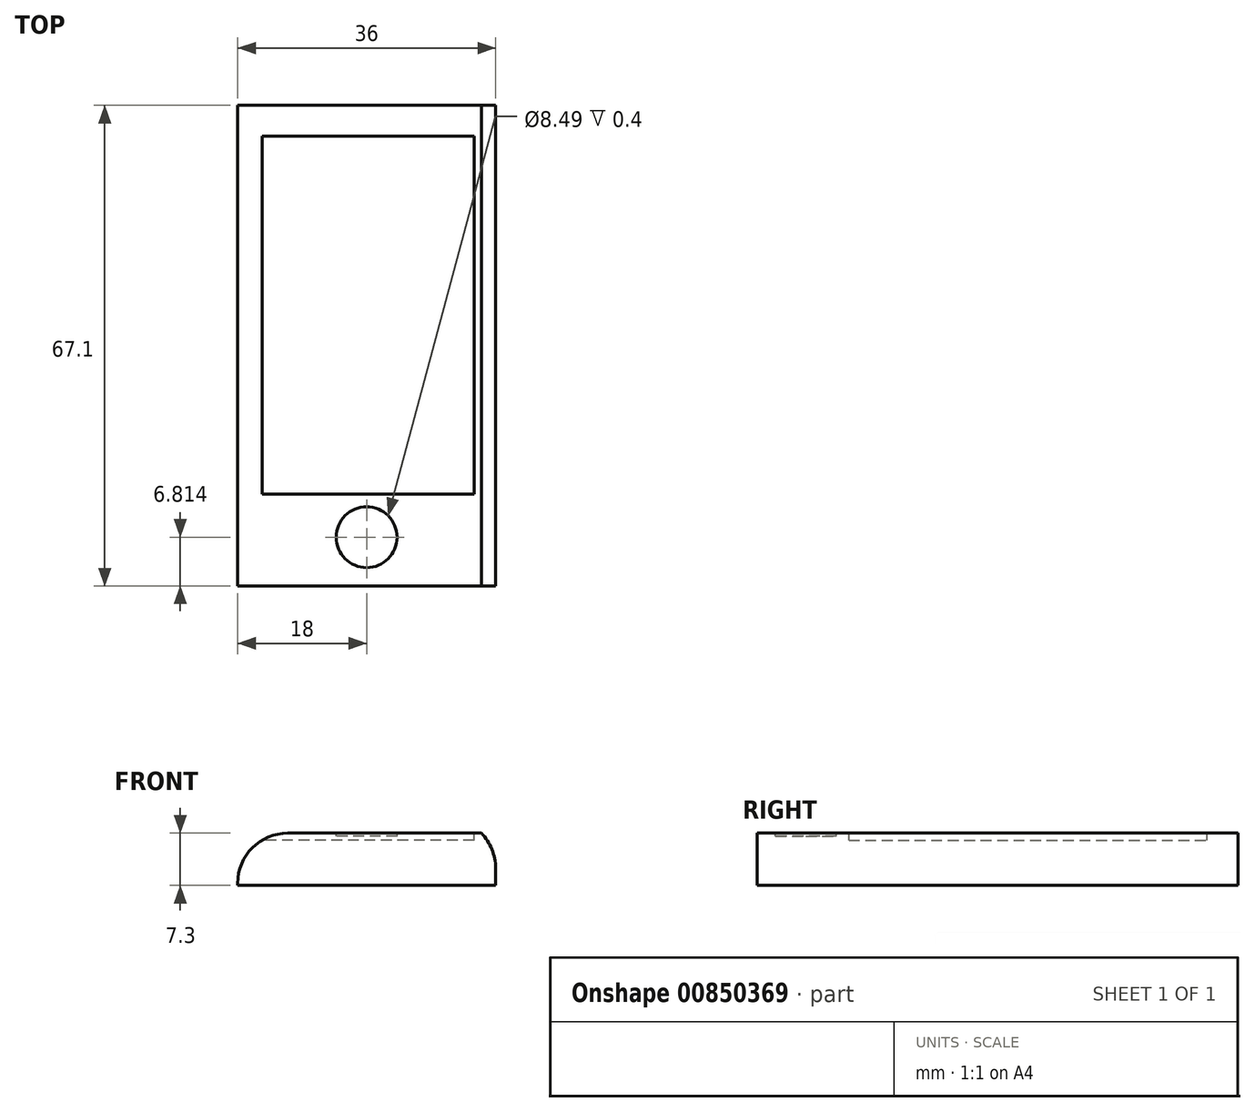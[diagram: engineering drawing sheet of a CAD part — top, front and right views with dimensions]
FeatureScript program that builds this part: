
annotation { "Feature Type Name" : "Feature", "Feature Type Description" : "" }
export const myFeature = defineFeature(function(context is Context, id is Id, definition is map)
    precondition{}
    {
        {
            var Q0;
            Q0=qCreatedBy(makeId("Top.planeOp"),FACE);
            var sketch = newSketch(context, id + "F0", { "sketchPlane" : qUnion([Q0])});
            skLineSegment(sketch, "E0.bottom", {"start": v(-18, 33.55) * mm, "end": v(18, 33.55) * mm});
            skLineSegment(sketch, "E0.top", {"start": v(-18, -33.55) * mm, "end": v(18, -33.55) * mm});
            skLineSegment(sketch, "E0.left", {"start": v(-18, 33.55) * mm, "end": v(-18, -33.55) * mm});
            skLineSegment(sketch, "E0.right", {"start": v(18, 33.55) * mm, "end": v(18, -33.55) * mm});
            skPoint(sketch, "E0.middle", {"position": v(0, 0) * mm});
            skSolve(sketch);
        }
        {
            var Q0;
            Q0=qSketchRegion(id+"F0",true);
            extrude(context, id + "F1", {"entities" : qUnion([Q0]), "depth" : 7.3 * mm, "offsetDistance" : 25 * mm});
        }
        {
            var Q0;
            Q0=makeQuery(id+"F1.opExtrude","CAP_FACE",FACE,{"disambiguationData":[OSD([sQuery(id+"F0.wireOp",EDGE,"E0.bottom"),sQuery(id+"F0.wireOp",EDGE,"E0.top"),sQuery(id+"F0.wireOp",EDGE,"E0.left"),sQuery(id+"F0.wireOp",EDGE,"E0.right")])],"isStart":false});
            var sketch = newSketch(context, id + "F2", { "sketchPlane" : qUnion([Q0])});
            skCircle(sketch, "E1", {"center": v(0, -26.74) * mm, "radius": 4.25 * mm});
            skSolve(sketch);
        }
        {
            var Q0;
            Q0=qSketchRegion(id+"F2",true);
            extrude(context, id + "F3", {"entities" : qUnion([Q0]), "operationType" : NewBodyOperationType.REMOVE, "oppositeDirection" : true, "depth" : 0.4 * mm, "offsetDistance" : 25 * mm});
        }
        {
            var Q0;
            Q0=makeQuery(id+"F2.imprint","IMPRINT",FACE,{"disambiguationData":[TD([[makeQuery(id+"F2.imprint","IMPRINT",EDGE,{"derivedFrom":sQuery(id+"F2.wireOp",EDGE,"E1")}),-1.0]])]});
            var sketch = newSketch(context, id + "F4", { "sketchPlane" : qUnion([Q0])});
            skLineSegment(sketch, "E2.bottom", {"start": v(15, -20.74) * mm, "end": v(-15, -20.74) * mm});
            skLineSegment(sketch, "E2.top", {"start": v(15, 29.26) * mm, "end": v(-15, 29.26) * mm});
            skLineSegment(sketch, "E2.left", {"start": v(15, -20.74) * mm, "end": v(15, 29.26) * mm});
            skLineSegment(sketch, "E2.right", {"start": v(-15, -20.74) * mm, "end": v(-15, 29.26) * mm});
            skPoint(sketch, "E2.middle", {"position": v(0, 4.26) * mm});
            skSolve(sketch);
        }
        {
            var Q0;
            Q0=makeQuery(id+"F1.opExtrude","CAP_EDGE",EDGE,{"disambiguationData":[OSD([sQuery(id+"F0.wireOp",EDGE,"E0.right")])],"isStart":false});
            chamfer(context, id + "F5", {"entities" : qUnion([Q0]), "width" : 2 * mm, "tangentPropagation" : true});
        }
        {
            var Q0;
            {var subQ0=sQuery(id+"F0.wireOp",EDGE,"E0.right");Q0=makeQuery(id+"F5.opChamfer","BLEND_EDGE",EDGE,{"blendedFrom":[makeQuery(id+"F1.opExtrude","CAP_EDGE",EDGE,{"disambiguationData":[OSD([subQ0])],"isStart":false}),makeQuery(id+"F1.opExtrude","SWEPT_FACE",FACE,{"disambiguationData":[OSD([subQ0])]})],"blendedInto":[makeQuery(id+"F1.opExtrude","SWEPT_FACE",FACE,{"disambiguationData":[OSD([subQ0])]})]});}
            fillet(context, id + "F6", {"entities" : qUnion([Q0]), "radius" : 7 * mm, "tangentPropagation" : true, "allowEdgeOverflow" : false});
        }
        {
            var Q0;
            Q0=qSketchRegion(id+"F4",true);
            extrude(context, id + "F7", {"entities" : qUnion([Q0]), "operationType" : NewBodyOperationType.REMOVE, "oppositeDirection" : true, "depth" : 1 * mm, "offsetDistance" : 25 * mm});
        }
        {
            var Q0;
            Q0=makeQuery(id+"F1.opExtrude","CAP_EDGE",EDGE,{"disambiguationData":[OSD([sQuery(id+"F0.wireOp",EDGE,"E0.left")])],"isStart":false});
            fillet(context, id + "F8", {"entities" : qUnion([Q0]), "radius" : 7 * mm, "tangentPropagation" : true, "allowEdgeOverflow" : false});
        }
    });
